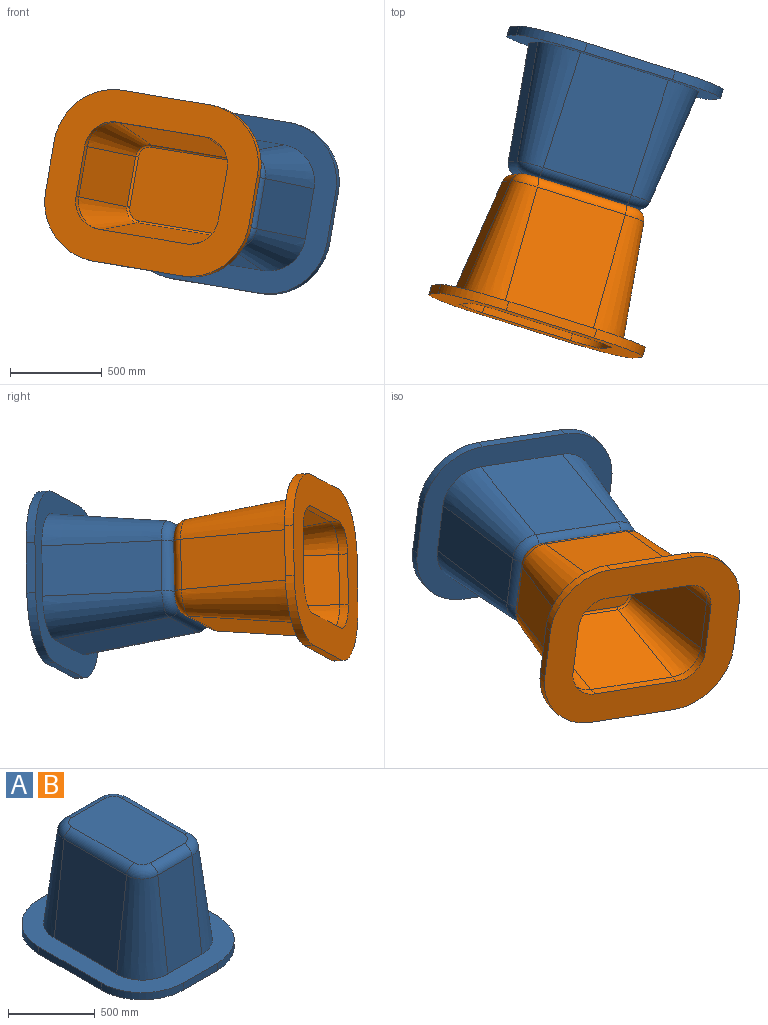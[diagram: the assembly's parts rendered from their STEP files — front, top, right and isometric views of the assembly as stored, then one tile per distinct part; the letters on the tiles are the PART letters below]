
ASSEMBLY  parts=2 mates=1
PART A: 52 faces, bbox 944.2x1175.5x762.7 mm
  f0: plane 649.9x277.42mm, normal (0,-0.99,-0.12), area 181649.3mm2, adj f5,f8,f14,f33
  f1: plane 649.9x508.76mm, normal (0.99,0,-0.12), area 333129.1mm2, adj f5,f6,f15,f19
  f2: plane 649.9x277.42mm, normal (0,0.99,-0.12), area 181649.3mm2, adj f6,f7,f11,f21
  f3: plane 649.9x508.76mm, normal (-0.99,0,-0.12), area 333129.1mm2, adj f7,f8,f10,f23
  f4: plane 638.69x407.35mm, normal (0,0,-1), area 256545.6mm2, adj f9,f10,f11,f12,f13,f14,f15,f16
  f5: cone r=76.2mm half-angle=7deg, axis (0,0,-1), area 120819.9mm2, adj f0,f1,f16,f18
  f6: cone r=76.2mm half-angle=7deg, axis (0,0,-1), area 120819.9mm2, adj f1,f2,f13,f20
  f7: cone r=76.2mm half-angle=7deg, axis (0,0,-1), area 120819.9mm2, adj f2,f3,f9,f22
  f8: cone r=76.2mm half-angle=7deg, axis (0,0,-1), area 120819.9mm2, adj f0,f3,f12,f24
  f9: torus R=64.96mm, axis (0,0,1), area 2099.9mm2, adj f4,f7,f10,f11
  f10: cylinder r=12.7mm len=508.76mm, axis (0,-1,0), area 9360mm2, adj f3,f4,f9,f12
  f11: cylinder r=12.7mm len=277.42mm, axis (1,0,0), area 5103.8mm2, adj f2,f4,f9,f13
  f12: torus R=64.96mm, axis (0,0,1), area 2099.9mm2, adj f4,f8,f10,f14
  f13: torus R=64.96mm, axis (0,0,1), area 2099.9mm2, adj f4,f6,f11,f15
  f14: cylinder r=12.7mm len=277.42mm, axis (1,0,0), area 5103.8mm2, adj f0,f4,f12,f16
  f15: cylinder r=12.7mm len=508.76mm, axis (0,-1,0), area 9360mm2, adj f1,f4,f13,f16
  f16: torus R=64.96mm, axis (0,0,1), area 2099.9mm2, adj f4,f5,f14,f15
  f17: plane 1175.51x944.17mm, normal (0,0,1), area 409886.7mm2, adj f25,f26,f27,f28,f29,f30,f31,f32
  f18: cylinder r=157.37mm len=157.37mm, axis (0,0,1), area 12557.4mm2, adj f5,f19,f33,f34
  f19: plane 508.76x50.8mm, normal (1,0,0), area 25845.1mm2, adj f1,f18,f20,f34
  f20: cylinder r=157.37mm len=157.37mm, axis (0,0,1), area 12557.4mm2, adj f6,f19,f21,f34
  f21: plane 277.42x50.8mm, normal (0,1,0), area 14092.9mm2, adj f2,f20,f22,f34
  f22: cylinder r=157.37mm len=157.37mm, axis (0,0,1), area 12557.4mm2, adj f7,f21,f23,f34
  f23: plane 508.76x50.8mm, normal (-1,0,0), area 25845.1mm2, adj f3,f22,f24,f34
  f24: cylinder r=157.37mm len=157.37mm, axis (0,0,1), area 12557.4mm2, adj f8,f23,f33,f34
  f25: cylinder r=333.37mm len=333.37mm, axis (0,0,1), area 26602.1mm2, adj f17,f26,f32,f34
  f26: plane 508.76x50.8mm, normal (1,0,0), area 25845.1mm2, adj f17,f25,f27,f34
  f27: cylinder r=333.37mm len=333.37mm, axis (0,0,1), area 26602.1mm2, adj f17,f26,f28,f34
  f28: plane 277.42x50.8mm, normal (0,-1,0), area 14092.9mm2, adj f17,f27,f29,f34
  f29: cylinder r=333.37mm len=333.37mm, axis (0,0,1), area 26602.1mm2, adj f17,f28,f30,f34
  f30: plane 508.76x50.8mm, normal (-1,0,0), area 25845.1mm2, adj f17,f29,f31,f34
  f31: cylinder r=333.37mm len=333.37mm, axis (0,0,1), area 26602.1mm2, adj f17,f30,f32,f34
  f32: plane 277.42x50.8mm, normal (0,1,0), area 14092.9mm2, adj f17,f25,f31,f34
  f33: plane 277.42x50.8mm, normal (0,-1,0), area 14092.9mm2, adj f0,f18,f24,f34
  f34: plane 1175.51x944.17mm, normal (0,0,-1), area 548099.4mm2, adj f18,f19,f20,f21,f22,f23,f24,f25
  f35: plane 637.93x406.58mm, normal (0,0,1), area 255790.4mm2, adj f36,f37,f38,f39,f40,f41,f42,f43
  f36: cylinder r=63.5mm len=508.76mm, axis (0,-1,0), area 46799.8mm2, adj f35,f37,f43,f51
  f37: torus R=64.58mm, axis (0,0,1), area 14893.7mm2, adj f35,f36,f38,f50
  f38: cylinder r=63.5mm len=277.42mm, axis (1,0,0), area 25519.1mm2, adj f35,f37,f39,f49
  f39: torus R=64.58mm, axis (0,0,1), area 14893.7mm2, adj f35,f38,f40,f48
  f40: cylinder r=63.5mm len=508.76mm, axis (0,-1,0), area 46799.8mm2, adj f35,f39,f41,f47
  f41: torus R=64.58mm, axis (0,0,1), area 14893.7mm2, adj f35,f40,f42,f46
  f42: cylinder r=63.5mm len=277.42mm, axis (1,0,0), area 25519.1mm2, adj f35,f41,f43,f45
  f43: torus R=64.58mm, axis (0,0,1), area 14893.7mm2, adj f35,f36,f42,f44
  f44: cone r=127mm half-angle=7deg, axis (0,0,-1), area 174323.4mm2, adj f17,f43,f45,f51
  f45: plane 656.09x277.42mm, normal (0,-0.99,0.12), area 183379.7mm2, adj f17,f42,f44,f46
  f46: cone r=127mm half-angle=7deg, axis (0,0,-1), area 174323.4mm2, adj f17,f41,f45,f47
  f47: plane 656.09x508.76mm, normal (0.99,0,0.12), area 336302.5mm2, adj f17,f40,f46,f48
  f48: cone r=127mm half-angle=7deg, axis (0,0,-1), area 174323.4mm2, adj f17,f39,f47,f49
  f49: plane 656.09x277.42mm, normal (0,0.99,0.12), area 183379.7mm2, adj f17,f38,f48,f50
  f50: cone r=127mm half-angle=7deg, axis (0,0,-1), area 174323.4mm2, adj f17,f37,f49,f51
  f51: plane 656.09x508.76mm, normal (-0.99,0,0.12), area 336302.5mm2, adj f17,f36,f44,f50
PART B: same geometry as A
PLACE A rot(axis=(0.56,0.49,-0.67),134.5deg) t=(-480.77,-1735.88,-1783.25)mm
PLACE B rot(axis=(-0.69,-0.43,-0.58),126.5deg) t=(-170.23,-3031.36,2504.06)mm fixed
MATE fastened B.f35 <-> A.f35  axis (0.29,0.96,-0.06) through (-244.98,-2408.87,346.94)mm
